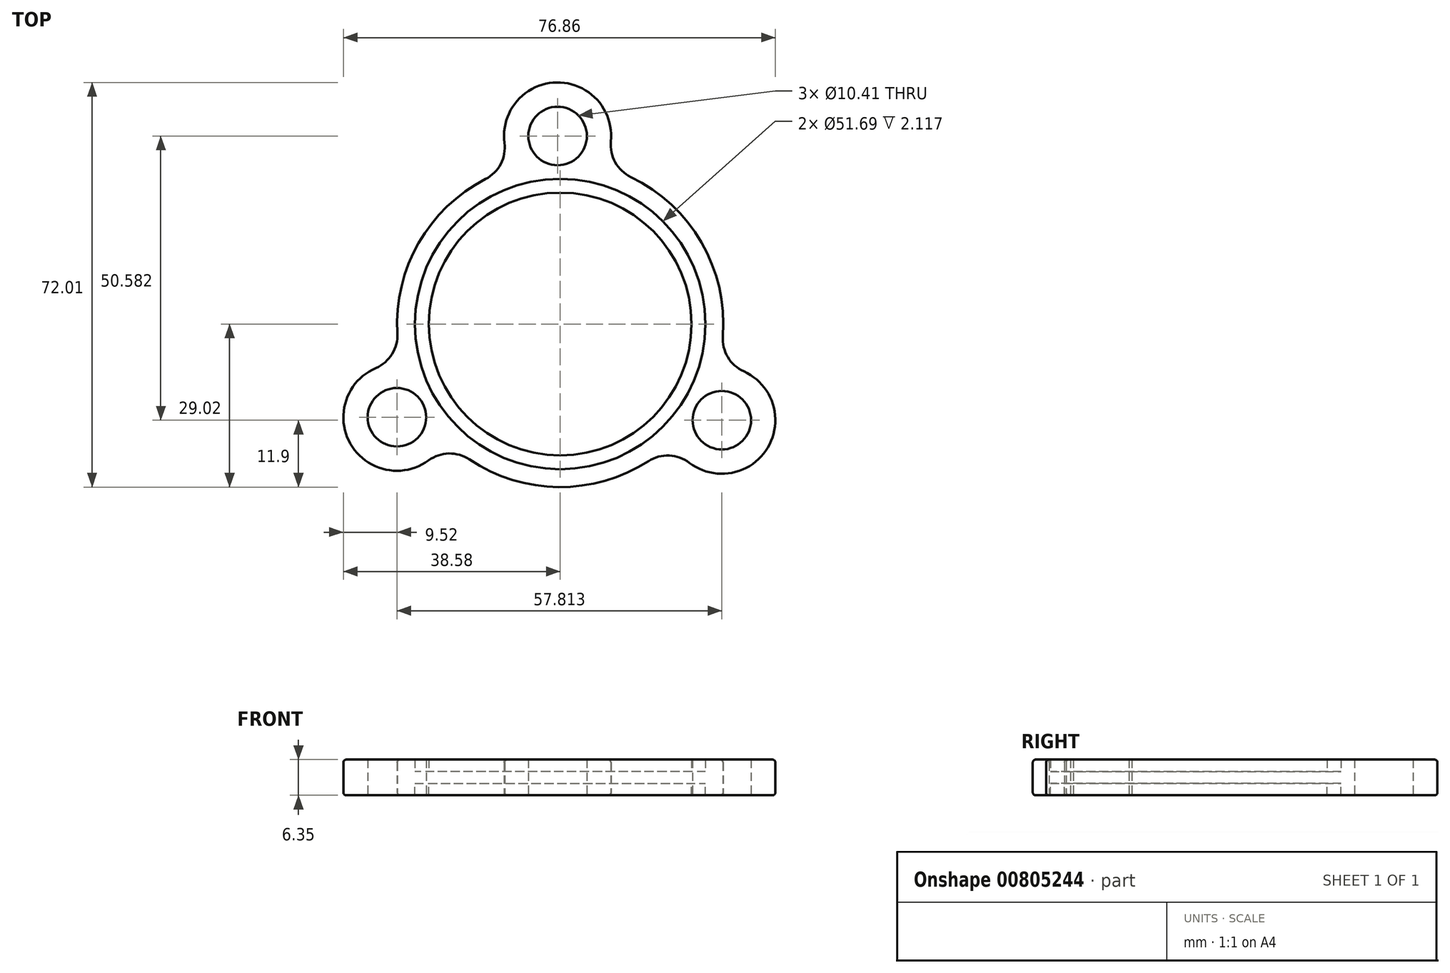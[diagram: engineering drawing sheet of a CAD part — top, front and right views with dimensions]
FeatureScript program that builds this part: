
annotation { "Feature Type Name" : "Feature", "Feature Type Description" : "" }
export const myFeature = defineFeature(function(context is Context, id is Id, definition is map)
    precondition{}
    {
        {
            var Q0;
            Q0=qCreatedBy(makeId("Top.planeOp"),FACE);
            var sketch = newSketch(context, id + "F0", { "sketchPlane" : qUnion([Q0])});
            skCircle(sketch, "E0", {"center": v(0, 0) * mm, "radius": 25.84 * mm});
            skCircle(sketch, "E1", {"center": v(0, 0) * mm, "radius": 23.37 * mm});
            skLineSegment(sketch, "E2", {"start": v(0, 62.71) * mm, "end": v(-0.39, 38.67) * mm});
            skCircle(sketch, "E3", {"center": v(-0.47, 33.46) * mm, "radius": 5.2 * mm});
            skCircle(sketch, "E4", {"center": v(28.75, -17.12) * mm, "radius": 5.2 * mm});
            skArc(sketch, "E5", {"start": v(-32.81, -7.84) * mm, "mid": v(-37.33, -21.32) * mm, "end": v(-23.43, -24.28) * mm});
            skCircle(sketch, "E6", {"center": v(-29.06, -16.6) * mm, "radius": 5.2 * mm});
            skArc(sketch, "E7", {"start": v(9, 32.51) * mm, "mid": v(-0.6, 42.99) * mm, "end": v(-9.92, 32.25) * mm});
            skArc(sketch, "E8", {"start": v(22.98, -24.7) * mm, "mid": v(36.94, -22) * mm, "end": v(32.66, -8.43) * mm});
            skLineSegment(sketch, "E9.trimOffspring", {"start": v(37, -21.88) * mm, "end": v(57.9, -34.4) * mm});
            skPoint(sketch, "E10.visualSharp", {"position": v(32.39, -8.32) * mm});
            skPoint(sketch, "E11.visualSharp", {"position": v(22.95, -24.67) * mm});
            skPoint(sketch, "E12.visualSharp", {"position": v(8.97, 32.2) * mm});
            skPoint(sketch, "E13.visualSharp", {"position": v(-9.91, 32.2) * mm});
            skPoint(sketch, "E14.visualSharp", {"position": v(-32.7, -7.8) * mm});
            skPoint(sketch, "E15.visualSharp", {"position": v(-23.25, -24.14) * mm});
            skArc(sketch, "E16", {"start": v(-13.3, 25.8) * mm, "mid": v(-25.2, 14.4) * mm, "end": v(-28.97, -1.64) * mm});
            skArc(sketch, "E17.trimOffspring", {"start": v(28.94, -2.17) * mm, "mid": v(25.13, 14.52) * mm, "end": v(12.58, 26.15) * mm});
            skArc(sketch, "E18.trimOffspring", {"start": v(-16.14, -24.12) * mm, "mid": v(-0.26, -29.02) * mm, "end": v(15.7, -24.4) * mm});
            skPoint(sketch, "E19.visualSharp", {"position": v(-8.16, 27.85) * mm});
            skArc(sketch, "E19.filletArc", {"start": v(-13.3, 25.8) * mm, "mid": v(-10.6, 28.48) * mm, "end": v(-9.92, 32.25) * mm});
            skPoint(sketch, "E20.visualSharp", {"position": v(7.38, 28.07) * mm});
            skArc(sketch, "E20.filletArc", {"start": v(9, 32.51) * mm, "mid": v(9.79, 28.77) * mm, "end": v(12.58, 26.15) * mm});
            skPoint(sketch, "E21.visualSharp", {"position": v(28, -7.63) * mm});
            skArc(sketch, "E21.filletArc", {"start": v(28.94, -2.17) * mm, "mid": v(29.81, -5.9) * mm, "end": v(32.66, -8.43) * mm});
            skPoint(sketch, "E22.visualSharp", {"position": v(20.05, -20.98) * mm});
            skArc(sketch, "E22.filletArc", {"start": v(22.98, -24.7) * mm, "mid": v(19.39, -23.4) * mm, "end": v(15.7, -24.4) * mm});
            skPoint(sketch, "E23.visualSharp", {"position": v(-20.42, -20.61) * mm});
            skArc(sketch, "E23.filletArc", {"start": v(-16.14, -24.12) * mm, "mid": v(-19.8, -23.05) * mm, "end": v(-23.43, -24.28) * mm});
            skPoint(sketch, "E24.visualSharp", {"position": v(-28.13, -7.12) * mm});
            skArc(sketch, "E24.filletArc", {"start": v(-32.81, -7.84) * mm, "mid": v(-29.91, -5.35) * mm, "end": v(-28.97, -1.64) * mm});
            skSolve(sketch);
        }
        {
            var Q0;
            Q0=qCreatedBy(makeId("Top.planeOp"),FACE);
            var sketch = newSketch(context, id + "F1", { "sketchPlane" : qUnion([Q0])});
            skSolve(sketch);
        }
        {
            var Q0;
            Q0 = qSketchRegion(id + "F1", true);
            var Q1;
            Q1=makeQuery(id+"F0.imprint","IMPRINT",FACE,{"disambiguationData":[TD([[makeQuery(id+"F0.imprint","IMPRINT",EDGE,{"derivedFrom":sQuery(id+"F0.wireOp",EDGE,"E1")}),1.0]])]});
            var Q2;
            Q2=makeQuery(id+"F0.imprint","IMPRINT",FACE,{"disambiguationData":[TD([[makeQuery(id+"F0.imprint","IMPRINT",EDGE,{"derivedFrom":sQuery(id+"F0.wireOp",EDGE,"E0")}),-1.0]])]});
            extrude(context, id + "F2", {"entities" : qUnion([Q0, Q1, Q2]), "depth" : 2.12 * mm, "offsetDistance" : 25.4 * mm});
        }
        {
            var Q0;
            Q0=makeQuery(id+"F2.opExtrude","CAP_FACE",FACE,{"disambiguationData":[OSD([sQuery(id+"F0.wireOp",EDGE,"E0"),sQuery(id+"F0.wireOp",EDGE,"E3"),sQuery(id+"F0.wireOp",EDGE,"E4"),sQuery(id+"F0.wireOp",EDGE,"E5"),sQuery(id+"F0.wireOp",EDGE,"E6"),sQuery(id+"F0.wireOp",EDGE,"E7"),sQuery(id+"F0.wireOp",EDGE,"E8"),sQuery(id+"F0.wireOp",EDGE,"E16"),sQuery(id+"F0.wireOp",EDGE,"E17.trimOffspring"),sQuery(id+"F0.wireOp",EDGE,"E18.trimOffspring"),sQuery(id+"F0.wireOp",EDGE,"E19.filletArc"),sQuery(id+"F0.wireOp",EDGE,"E20.filletArc"),sQuery(id+"F0.wireOp",EDGE,"E21.filletArc"),sQuery(id+"F0.wireOp",EDGE,"E22.filletArc"),sQuery(id+"F0.wireOp",EDGE,"E23.filletArc"),sQuery(id+"F0.wireOp",EDGE,"E24.filletArc")])],"isStart":true});
            var sketch = newSketch(context, id + "F3", { "sketchPlane" : qUnion([Q0])});
            skSolve(sketch);
        }
        {
            var Q0;
            Q0=makeQuery(id+"F3.imprint","IMPRINT",FACE,{"disambiguationData":[TD([[makeQuery(id+"F3.imprint","IMPRINT",EDGE,{"derivedFrom":makeQuery(id+"F2.opExtrude","CAP_EDGE",EDGE,{"disambiguationData":[OSD([sQuery(id+"F0.wireOp",EDGE,"E0")])],"isStart":true})}),1.0]])]});
            var Q1;
            Q1=makeQuery(id+"F3.imprint","IMPRINT",FACE,{"disambiguationData":[TD([[makeQuery(id+"F3.imprint","IMPRINT",EDGE,{"derivedFrom":makeQuery(id+"F2.opExtrude","CAP_EDGE",EDGE,{"disambiguationData":[OSD([sQuery(id+"F0.wireOp",EDGE,"E0")])],"isStart":true})}),-1.0]])]});
            extrude(context, id + "F4", {"entities" : qUnion([Q0, Q1]), "operationType" : NewBodyOperationType.ADD, "depth" : 2.12 * mm, "offsetDistance" : 25.4 * mm});
        }
        {
            var Q0;
            Q0=makeQuery(id+"F4.opExtrude","CAP_FACE",FACE,{"disambiguationData":[OSD([sQuery(id+"F0.wireOp",EDGE,"E3"),sQuery(id+"F0.wireOp",EDGE,"E4"),sQuery(id+"F0.wireOp",EDGE,"E5"),sQuery(id+"F0.wireOp",EDGE,"E6"),sQuery(id+"F0.wireOp",EDGE,"E7"),sQuery(id+"F0.wireOp",EDGE,"E8"),sQuery(id+"F0.wireOp",EDGE,"E16"),sQuery(id+"F0.wireOp",EDGE,"E17.trimOffspring"),sQuery(id+"F0.wireOp",EDGE,"E18.trimOffspring"),sQuery(id+"F0.wireOp",EDGE,"E19.filletArc"),sQuery(id+"F0.wireOp",EDGE,"E20.filletArc"),sQuery(id+"F0.wireOp",EDGE,"E21.filletArc"),sQuery(id+"F0.wireOp",EDGE,"E22.filletArc"),sQuery(id+"F0.wireOp",EDGE,"E23.filletArc"),sQuery(id+"F0.wireOp",EDGE,"E24.filletArc")])],"isStart":false});
            var sketch = newSketch(context, id + "F5", { "sketchPlane" : qUnion([Q0])});
            skCircle(sketch, "E25.0", {"center": v(0, 0) * mm, "radius": 23.37 * mm});
            skCircle(sketch, "E26.0", {"center": v(0, 0) * mm, "radius": 25.84 * mm});
            skArc(sketch, "E27.0.0", {"start": v(22.98, 24.7) * mm, "mid": v(36.94, 22) * mm, "end": v(32.66, 8.43) * mm});
            skArc(sketch, "E27.0.1", {"start": v(32.66, 8.43) * mm, "mid": v(29.81, 5.9) * mm, "end": v(28.94, 2.17) * mm});
            skArc(sketch, "E27.0.2", {"start": v(28.94, 2.17) * mm, "mid": v(25.13, -14.52) * mm, "end": v(12.58, -26.15) * mm});
            skArc(sketch, "E27.0.3", {"start": v(12.58, -26.15) * mm, "mid": v(9.79, -28.77) * mm, "end": v(9, -32.51) * mm});
            skArc(sketch, "E27.0.4", {"start": v(9, -32.51) * mm, "mid": v(-0.6, -42.99) * mm, "end": v(-9.92, -32.25) * mm});
            skArc(sketch, "E27.0.5", {"start": v(-9.92, -32.25) * mm, "mid": v(-10.6, -28.48) * mm, "end": v(-13.3, -25.8) * mm});
            skArc(sketch, "E27.0.6", {"start": v(-13.3, -25.8) * mm, "mid": v(-25.2, -14.4) * mm, "end": v(-28.97, 1.64) * mm});
            skArc(sketch, "E27.0.7", {"start": v(-28.97, 1.64) * mm, "mid": v(-29.91, 5.35) * mm, "end": v(-32.81, 7.84) * mm});
            skArc(sketch, "E27.0.8", {"start": v(-32.81, 7.84) * mm, "mid": v(-37.33, 21.32) * mm, "end": v(-23.43, 24.28) * mm});
            skArc(sketch, "E27.0.9", {"start": v(-23.43, 24.28) * mm, "mid": v(-19.8, 23.05) * mm, "end": v(-16.14, 24.12) * mm});
            skArc(sketch, "E27.0.10", {"start": v(-16.14, 24.12) * mm, "mid": v(-0.26, 29.02) * mm, "end": v(15.7, 24.4) * mm});
            skArc(sketch, "E27.0.11", {"start": v(15.7, 24.4) * mm, "mid": v(19.39, 23.4) * mm, "end": v(22.98, 24.7) * mm});
            skSolve(sketch);
        }
        {
            var Q0;
            Q0=makeQuery(id+"F5.imprint","IMPRINT",FACE,{"disambiguationData":[TD([[makeQuery(id+"F5.imprint","IMPRINT",EDGE,{"derivedFrom":sQuery(id+"F5.wireOp",EDGE,"E25.0")}),1.0]])]});
            var Q1;
            Q1=makeQuery(id+"F5.imprint","IMPRINT",FACE,{"disambiguationData":[TD([[makeQuery(id+"F5.imprint","IMPRINT",EDGE,{"derivedFrom":sQuery(id+"F5.wireOp",EDGE,"E26.0")}),-1.0]])]});
            extrude(context, id + "F6", {"entities" : qUnion([Q0, Q1]), "operationType" : NewBodyOperationType.ADD, "depth" : 2.12 * mm, "offsetDistance" : 25.4 * mm});
        }
        {
            var Q0;
            Q0=makeQuery(id+"F2.opExtrude","CAP_EDGE",EDGE,{"disambiguationData":[OSD([sQuery(id+"F0.wireOp",EDGE,"E20.filletArc")])],"isStart":false});
            var Q1;
            Q1=makeQuery(id+"F6.opExtrude","CAP_EDGE",EDGE,{"disambiguationData":[OSD([sQuery(id+"F5.wireOp",EDGE,"E27.0.2")])],"isStart":false});
            fillet(context, id + "F7", {"entities" : qUnion([Q0, Q1]), "radius" : 0.5 * mm, "tangentPropagation" : true, "allowEdgeOverflow" : false});
        }
    });
